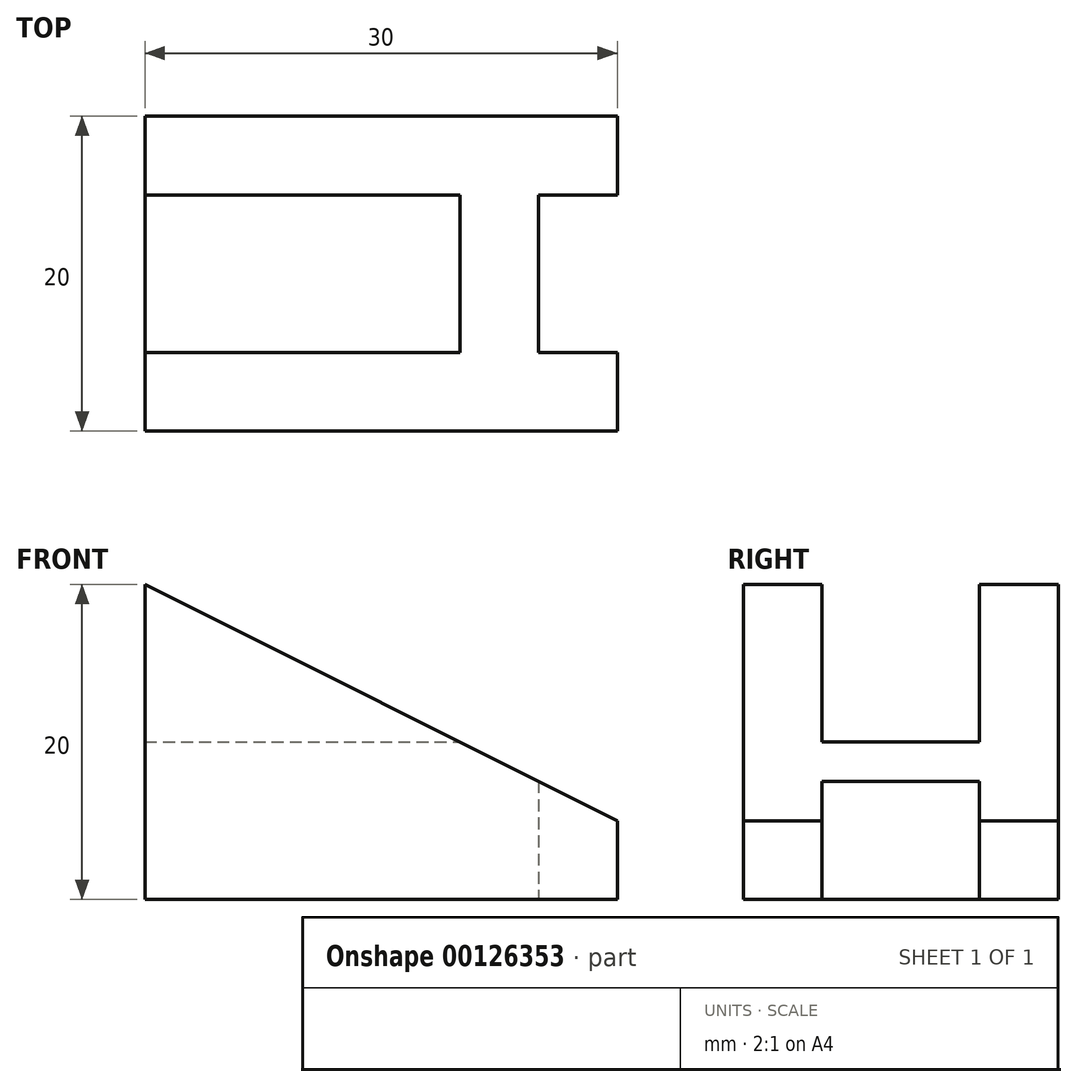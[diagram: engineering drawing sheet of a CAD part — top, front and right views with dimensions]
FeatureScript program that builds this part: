
annotation { "Feature Type Name" : "Feature", "Feature Type Description" : "" }
export const myFeature = defineFeature(function(context is Context, id is Id, definition is map)
    precondition{}
    {
        {
            var Q0;
            Q0=qCreatedBy(makeId("Front.planeOp"),FACE);
            var sketch = newSketch(context, id + "F0", { "sketchPlane" : qUnion([Q0])});
            skLineSegment(sketch, "E0.bottom", {"start": v(0, 0) * mm, "end": v(-30, 0) * mm});
            skLineSegment(sketch, "E0.top", {"start": v(0, 20) * mm, "end": v(-30, 20) * mm});
            skLineSegment(sketch, "E0.left", {"start": v(0, 0) * mm, "end": v(0, 20) * mm});
            skLineSegment(sketch, "E0.right", {"start": v(-30, 0) * mm, "end": v(-30, 20) * mm});
            skSolve(sketch);
        }
        {
            var Q0;
            Q0 = qSketchRegion(id + "F0", true);
            extrude(context, id + "F1", {"entities" : qUnion([Q0]), "oppositeDirection" : true, "depth" : 20 * mm});
        }
        {
            var Q0;
            Q0=qCreatedBy(makeId("Front.planeOp"),FACE);
            var sketch = newSketch(context, id + "F2", { "sketchPlane" : qUnion([Q0])});
            skLineSegment(sketch, "E1", {"start": v(0, 5) * mm, "end": v(-30, 20) * mm});
            skLineSegment(sketch, "E2", {"start": v(0, 5) * mm, "end": v(0, 20) * mm});
            skLineSegment(sketch, "E3", {"start": v(0, 20) * mm, "end": v(-30, 20) * mm});
            skSolve(sketch);
        }
        {
            var Q0;
            Q0 = qSketchRegion(id + "F2", true);
            extrude(context, id + "F3", {"entities" : qUnion([Q0]), "operationType" : NewBodyOperationType.REMOVE, "endBound" : BoundingType.THROUGH_ALL, "oppositeDirection" : true, "depth" : 25 * mm});
        }
        {
            var Q0;
            Q0=qCreatedBy(makeId("Right.planeOp"),FACE);
            var sketch = newSketch(context, id + "F4", { "sketchPlane" : qUnion([Q0])});
            skLineSegment(sketch, "E4.0.0", {"start": v(20, 5) * mm, "end": v(20, 20) * mm, "construction": true});
            skLineSegment(sketch, "E4.0.1", {"start": v(20, 20) * mm, "end": v(0, 20) * mm, "construction": true});
            skLineSegment(sketch, "E4.0.2", {"start": v(0, 20) * mm, "end": v(0, 5) * mm, "construction": true});
            skLineSegment(sketch, "E4.0.3", {"start": v(0, 5) * mm, "end": v(20, 5) * mm, "construction": true});
            skPoint(sketch, "E5", {"position": v(5, 20) * mm});
            skPoint(sketch, "E6", {"position": v(5, 10) * mm});
            skLineSegment(sketch, "E7", {"start": v(5, 10) * mm, "end": v(5, 20) * mm});
            skLineSegment(sketch, "E8", {"start": v(15, 20) * mm, "end": v(15, 10) * mm});
            skLineSegment(sketch, "E9", {"start": v(15, 10) * mm, "end": v(5, 10) * mm});
            skLineSegment(sketch, "E10", {"start": v(5, 20) * mm, "end": v(15, 20) * mm});
            skSolve(sketch);
        }
        {
            var Q0;
            Q0 = qSketchRegion(id + "F4", true);
            extrude(context, id + "F5", {"entities" : qUnion([Q0]), "operationType" : NewBodyOperationType.REMOVE, "endBound" : BoundingType.THROUGH_ALL, "oppositeDirection" : true, "depth" : 25 * mm});
        }
        {
            var Q0;
            Q0=qCreatedBy(makeId("Top.planeOp"),FACE);
            var sketch = newSketch(context, id + "F6", { "sketchPlane" : qUnion([Q0])});
            skPoint(sketch, "E11", {"position": v(0, 5) * mm});
            skPoint(sketch, "E12", {"position": v(0, 15) * mm});
            skPoint(sketch, "E13", {"position": v(-5, 15) * mm});
            skPoint(sketch, "E14", {"position": v(-5, 5) * mm});
            skLineSegment(sketch, "E15.0.0", {"start": v(-10, 15) * mm, "end": v(-10, 5) * mm, "construction": true});
            skLineSegment(sketch, "E15.0.1", {"start": v(-10, 5) * mm, "end": v(-30, 5) * mm, "construction": true});
            skLineSegment(sketch, "E15.0.2", {"start": v(-30, 5) * mm, "end": v(-30, 0) * mm, "construction": true});
            skLineSegment(sketch, "E15.0.3", {"start": v(-30, 0) * mm, "end": v(0, 0) * mm, "construction": true});
            skLineSegment(sketch, "E15.0.4", {"start": v(0, 0) * mm, "end": v(0, 20) * mm, "construction": true});
            skLineSegment(sketch, "E15.0.5", {"start": v(0, 20) * mm, "end": v(-30, 20) * mm, "construction": true});
            skLineSegment(sketch, "E15.0.6", {"start": v(-30, 20) * mm, "end": v(-30, 15) * mm, "construction": true});
            skLineSegment(sketch, "E15.0.7", {"start": v(-30, 15) * mm, "end": v(-10, 15) * mm, "construction": true});
            skLineSegment(sketch, "E16", {"start": v(0, 5) * mm, "end": v(0, 15) * mm});
            skLineSegment(sketch, "E17", {"start": v(-5, 15) * mm, "end": v(-5, 5) * mm});
            skLineSegment(sketch, "E18", {"start": v(-5, 5) * mm, "end": v(0, 5) * mm});
            skLineSegment(sketch, "E19", {"start": v(-5, 15) * mm, "end": v(0, 15) * mm});
            skSolve(sketch);
        }
        {
            var Q0;
            Q0 = qSketchRegion(id + "F6", true);
            extrude(context, id + "F7", {"entities" : qUnion([Q0]), "operationType" : NewBodyOperationType.REMOVE, "endBound" : BoundingType.THROUGH_ALL, "depth" : 25 * mm});
        }
    });
